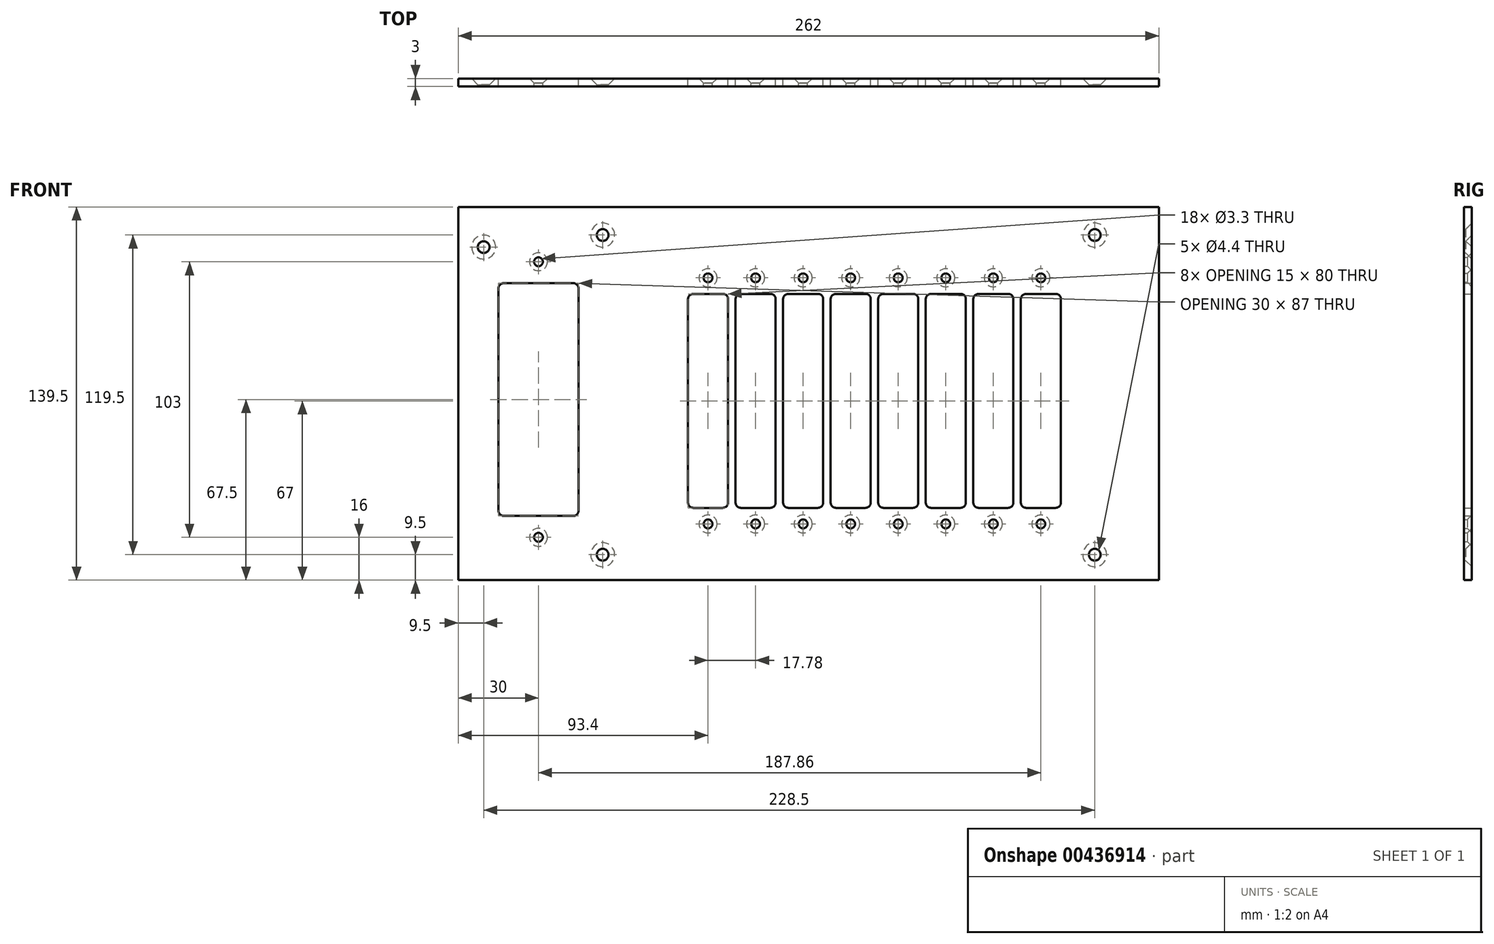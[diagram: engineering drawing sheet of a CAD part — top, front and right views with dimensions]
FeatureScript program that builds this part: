
annotation { "Feature Type Name" : "Feature", "Feature Type Description" : "" }
export const myFeature = defineFeature(function(context is Context, id is Id, definition is map)
    precondition{}
    {
        {
            var Q0;
            Q0=qCreatedBy(makeId("Front.planeOp"),FACE);
            var sketch = newSketch(context, id + "F0", { "sketchPlane" : qUnion([Q0])});
            skLineSegment(sketch, "E0.bottom", {"start": v(0, 0) * mm, "end": v(262, 0) * mm});
            skLineSegment(sketch, "E0.top", {"start": v(0, 139.5) * mm, "end": v(262, 139.5) * mm});
            skLineSegment(sketch, "E0.left", {"start": v(0, 0) * mm, "end": v(0, 139.5) * mm});
            skLineSegment(sketch, "E0.right", {"start": v(262, 0) * mm, "end": v(262, 139.5) * mm});
            skSolve(sketch);
        }
        {
            var Q0;
            Q0 = qSketchRegion(id + "F0", true);
            extrude(context, id + "F1", {"entities" : qUnion([Q0]), "depth" : 3 * mm});
        }
        {
            var Q0;
            Q0=makeQuery(id+"F1.opExtrude","CAP_FACE",FACE,{"disambiguationData":[OSD([sQuery(id+"F0.wireOp",EDGE,"E0.bottom"),sQuery(id+"F0.wireOp",EDGE,"E0.top"),sQuery(id+"F0.wireOp",EDGE,"E0.left"),sQuery(id+"F0.wireOp",EDGE,"E0.right"),sQuery(id+"F0.wireOp",EDGE,"e1765bbd-f1bd-4e84-b2cc-b87809b0bcc8.filletArc"),sQuery(id+"F0.wireOp",EDGE,"772ad9d4-1fb5-4f70-b089-cda75f8246e0.filletArc"),sQuery(id+"F0.wireOp",EDGE,"797730b0-c818-4667-b5a7-0f50415be0c5.filletArc"),sQuery(id+"F0.wireOp",EDGE,"a02b4f8d-2679-4b7b-95b5-bbf4c60ec907.filletArc")])],"isStart":true});
            var sketch = newSketch(context, id + "F2", { "sketchPlane" : qUnion([Q0])});
            skLineSegment(sketch, "E1.bottom", {"start": v(-43, 111) * mm, "end": v(-17, 111) * mm});
            skLineSegment(sketch, "E1.top", {"start": v(-43, 24) * mm, "end": v(-17, 24) * mm});
            skLineSegment(sketch, "E1.left", {"start": v(-45, 109) * mm, "end": v(-45, 26) * mm});
            skLineSegment(sketch, "E1.right", {"start": v(-15, 109) * mm, "end": v(-15, 26) * mm});
            skPoint(sketch, "E2.visualSharp", {"position": v(-45, 111) * mm});
            skArc(sketch, "E2.filletArc", {"start": v(-43, 111) * mm, "mid": v(-44.41, 110.41) * mm, "end": v(-45, 109) * mm});
            skPoint(sketch, "E3.visualSharp", {"position": v(-15, 111) * mm});
            skArc(sketch, "E3.filletArc", {"start": v(-15, 109) * mm, "mid": v(-15.59, 110.41) * mm, "end": v(-17, 111) * mm});
            skPoint(sketch, "E4.visualSharp", {"position": v(-15, 24) * mm});
            skArc(sketch, "E4.filletArc", {"start": v(-17, 24) * mm, "mid": v(-15.59, 24.59) * mm, "end": v(-15, 26) * mm});
            skPoint(sketch, "E5.visualSharp", {"position": v(-45, 24) * mm});
            skArc(sketch, "E5.filletArc", {"start": v(-45, 26) * mm, "mid": v(-44.41, 24.59) * mm, "end": v(-43, 24) * mm});
            skLineSegment(sketch, "E6", {"start": v(-30, 111) * mm, "end": v(-30, 24) * mm});
            skSolve(sketch);
        }
        {
            var Q0;
            Q0 = qSketchRegion(id + "F2", true);
            extrude(context, id + "F3", {"entities" : qUnion([Q0]), "operationType" : NewBodyOperationType.REMOVE, "endBound" : BoundingType.THROUGH_ALL, "oppositeDirection" : true, "depth" : 25 * mm});
        }
        {
            var Q0;
            Q0=makeQuery(id+"F1.opExtrude","CAP_FACE",FACE,{"disambiguationData":[OSD([sQuery(id+"F0.wireOp",EDGE,"E0.bottom"),sQuery(id+"F0.wireOp",EDGE,"E0.top"),sQuery(id+"F0.wireOp",EDGE,"E0.left"),sQuery(id+"F0.wireOp",EDGE,"E0.right"),sQuery(id+"F0.wireOp",EDGE,"e1765bbd-f1bd-4e84-b2cc-b87809b0bcc8.filletArc"),sQuery(id+"F0.wireOp",EDGE,"772ad9d4-1fb5-4f70-b089-cda75f8246e0.filletArc"),sQuery(id+"F0.wireOp",EDGE,"797730b0-c818-4667-b5a7-0f50415be0c5.filletArc"),sQuery(id+"F0.wireOp",EDGE,"a02b4f8d-2679-4b7b-95b5-bbf4c60ec907.filletArc")])],"isStart":true});
            var sketch = newSketch(context, id + "F4", { "sketchPlane" : qUnion([Q0])});
            skPoint(sketch, "E7", {"position": v(-30, 119) * mm});
            skPoint(sketch, "E7.positionSnap0", {"position": v(-30, 111) * mm});
            skPoint(sketch, "E8", {"position": v(-30, 16) * mm});
            skPoint(sketch, "E8.positionSnap0", {"position": v(-30, 24) * mm});
            skSolve(sketch);
        }
        {
            var Q0;
            Q0=sQuery(id+"F4.wireOp",VERTEX,"E7");
            var Q1;
            Q1=sQuery(id+"F4.wireOp",VERTEX,"E8");
            var Q2;
            Q2=makeQuery(id+"F1.opExtrude","SWEPT_BODY",BODY,{"disambiguationData":[OSD([sQuery(id+"F0.wireOp",EDGE,"E0.bottom"),sQuery(id+"F0.wireOp",EDGE,"E0.top"),sQuery(id+"F0.wireOp",EDGE,"E0.left"),sQuery(id+"F0.wireOp",EDGE,"E0.right"),sQuery(id+"F0.wireOp",EDGE,"e1765bbd-f1bd-4e84-b2cc-b87809b0bcc8.filletArc"),sQuery(id+"F0.wireOp",EDGE,"772ad9d4-1fb5-4f70-b089-cda75f8246e0.filletArc"),sQuery(id+"F0.wireOp",EDGE,"797730b0-c818-4667-b5a7-0f50415be0c5.filletArc"),sQuery(id+"F0.wireOp",EDGE,"a02b4f8d-2679-4b7b-95b5-bbf4c60ec907.filletArc")])]});
            hole(context, id + "F5", {"style" : HoleStyle.C_SINK, "endStyle" : HoleEndStyle.THROUGH, "standardTappedOrClearance" : lookupTablePath({ "standard" : "ISO", "fit" : "Normal", "size" : "M3", "type" : "Clearance" }), "standardBlindInLast" : lookupTablePath({ "fit" : "Standard", "standard" : "ISO", "size" : "M3", "type" : "Clearance" }), "holeDiameter" : 3.3 * mm, "cSinkDiameter" : 6.72 * mm, "cSinkAngle" : 90 * degree, "isTappedThrough" : true, "tappedDepth" : 12 * mm, "tapClearance" : 3, "locations" : qUnion([Q0, Q1]), "scope" : qUnion([Q2])});
        }
        {
            var Q0;
            Q0=makeQuery(id+"F1.opExtrude","CAP_FACE",FACE,{"disambiguationData":[OSD([sQuery(id+"F0.wireOp",EDGE,"E0.bottom"),sQuery(id+"F0.wireOp",EDGE,"E0.top"),sQuery(id+"F0.wireOp",EDGE,"E0.left"),sQuery(id+"F0.wireOp",EDGE,"E0.right"),sQuery(id+"F0.wireOp",EDGE,"e1765bbd-f1bd-4e84-b2cc-b87809b0bcc8.filletArc"),sQuery(id+"F0.wireOp",EDGE,"772ad9d4-1fb5-4f70-b089-cda75f8246e0.filletArc"),sQuery(id+"F0.wireOp",EDGE,"797730b0-c818-4667-b5a7-0f50415be0c5.filletArc"),sQuery(id+"F0.wireOp",EDGE,"a02b4f8d-2679-4b7b-95b5-bbf4c60ec907.filletArc")])],"isStart":true});
            var sketch = newSketch(context, id + "F6", { "sketchPlane" : qUnion([Q0])});
            skLineSegment(sketch, "E9.bottom", {"start": v(-87.9, 27) * mm, "end": v(-98.9, 27) * mm});
            skLineSegment(sketch, "E9.top", {"start": v(-87.9, 107) * mm, "end": v(-98.9, 107) * mm});
            skLineSegment(sketch, "E9.left", {"start": v(-85.9, 29) * mm, "end": v(-85.9, 105) * mm});
            skLineSegment(sketch, "E9.right", {"start": v(-100.9, 29) * mm, "end": v(-100.9, 105) * mm});
            skPoint(sketch, "E10.visualSharp", {"position": v(-100.9, 107) * mm});
            skArc(sketch, "E10.filletArc", {"start": v(-98.9, 107) * mm, "mid": v(-100.31, 106.41) * mm, "end": v(-100.9, 105) * mm});
            skPoint(sketch, "E11.visualSharp", {"position": v(-85.9, 107) * mm});
            skArc(sketch, "E11.filletArc", {"start": v(-85.9, 105) * mm, "mid": v(-86.49, 106.41) * mm, "end": v(-87.9, 107) * mm});
            skPoint(sketch, "E12.visualSharp", {"position": v(-85.9, 27) * mm});
            skArc(sketch, "E12.filletArc", {"start": v(-87.9, 27) * mm, "mid": v(-86.49, 27.59) * mm, "end": v(-85.9, 29) * mm});
            skPoint(sketch, "E13.visualSharp", {"position": v(-100.9, 27) * mm});
            skArc(sketch, "E13.filletArc", {"start": v(-100.9, 29) * mm, "mid": v(-100.31, 27.59) * mm, "end": v(-98.9, 27) * mm});
            skLineSegment(sketch, "E14.1.0.0", {"start": v(-105.68, 107) * mm, "end": v(-116.68, 107) * mm});
            skLineSegment(sketch, "E14.1.0.1", {"start": v(-105.68, 27) * mm, "end": v(-116.68, 27) * mm});
            skPoint(sketch, "E14.1.0.2", {"position": v(-118.68, 107) * mm});
            skPoint(sketch, "E14.1.0.3", {"position": v(-103.68, 107) * mm});
            skPoint(sketch, "E14.1.0.4", {"position": v(-103.68, 27) * mm});
            skPoint(sketch, "E14.1.0.5", {"position": v(-118.68, 27) * mm});
            skLineSegment(sketch, "E14.1.0.6", {"start": v(-103.68, 29) * mm, "end": v(-103.68, 105) * mm});
            skLineSegment(sketch, "E14.1.0.7", {"start": v(-118.68, 29) * mm, "end": v(-118.68, 105) * mm});
            skArc(sketch, "E14.1.0.8", {"start": v(-116.68, 107) * mm, "mid": v(-118.1, 106.41) * mm, "end": v(-118.68, 105) * mm});
            skArc(sketch, "E14.1.0.9", {"start": v(-103.68, 105) * mm, "mid": v(-104.27, 106.41) * mm, "end": v(-105.68, 107) * mm});
            skArc(sketch, "E14.1.0.10", {"start": v(-105.68, 27) * mm, "mid": v(-104.27, 27.59) * mm, "end": v(-103.68, 29) * mm});
            skArc(sketch, "E14.1.0.11", {"start": v(-118.68, 29) * mm, "mid": v(-118.1, 27.59) * mm, "end": v(-116.68, 27) * mm});
            skLineSegment(sketch, "E14.2.0.0", {"start": v(-123.46, 107) * mm, "end": v(-134.46, 107) * mm});
            skLineSegment(sketch, "E14.2.0.1", {"start": v(-123.46, 27) * mm, "end": v(-134.46, 27) * mm});
            skPoint(sketch, "E14.2.0.2", {"position": v(-136.46, 107) * mm});
            skPoint(sketch, "E14.2.0.3", {"position": v(-121.46, 107) * mm});
            skPoint(sketch, "E14.2.0.4", {"position": v(-121.46, 27) * mm});
            skPoint(sketch, "E14.2.0.5", {"position": v(-136.46, 27) * mm});
            skLineSegment(sketch, "E14.2.0.6", {"start": v(-121.46, 29) * mm, "end": v(-121.46, 105) * mm});
            skLineSegment(sketch, "E14.2.0.7", {"start": v(-136.46, 29) * mm, "end": v(-136.46, 105) * mm});
            skArc(sketch, "E14.2.0.8", {"start": v(-134.46, 107) * mm, "mid": v(-135.87, 106.41) * mm, "end": v(-136.46, 105) * mm});
            skArc(sketch, "E14.2.0.9", {"start": v(-121.46, 105) * mm, "mid": v(-122.05, 106.41) * mm, "end": v(-123.46, 107) * mm});
            skArc(sketch, "E14.2.0.10", {"start": v(-123.46, 27) * mm, "mid": v(-122.05, 27.59) * mm, "end": v(-121.46, 29) * mm});
            skArc(sketch, "E14.2.0.11", {"start": v(-136.46, 29) * mm, "mid": v(-135.87, 27.59) * mm, "end": v(-134.46, 27) * mm});
            skLineSegment(sketch, "E14.3.0.0", {"start": v(-141.24, 107) * mm, "end": v(-152.24, 107) * mm});
            skLineSegment(sketch, "E14.3.0.1", {"start": v(-141.24, 27) * mm, "end": v(-152.24, 27) * mm});
            skPoint(sketch, "E14.3.0.2", {"position": v(-154.24, 107) * mm});
            skPoint(sketch, "E14.3.0.3", {"position": v(-139.24, 107) * mm});
            skPoint(sketch, "E14.3.0.4", {"position": v(-139.24, 27) * mm});
            skPoint(sketch, "E14.3.0.5", {"position": v(-154.24, 27) * mm});
            skLineSegment(sketch, "E14.3.0.6", {"start": v(-139.24, 29) * mm, "end": v(-139.24, 105) * mm});
            skLineSegment(sketch, "E14.3.0.7", {"start": v(-154.24, 29) * mm, "end": v(-154.24, 105) * mm});
            skArc(sketch, "E14.3.0.8", {"start": v(-152.24, 107) * mm, "mid": v(-153.65, 106.41) * mm, "end": v(-154.24, 105) * mm});
            skArc(sketch, "E14.3.0.9", {"start": v(-139.24, 105) * mm, "mid": v(-139.83, 106.41) * mm, "end": v(-141.24, 107) * mm});
            skArc(sketch, "E14.3.0.10", {"start": v(-141.24, 27) * mm, "mid": v(-139.83, 27.59) * mm, "end": v(-139.24, 29) * mm});
            skArc(sketch, "E14.3.0.11", {"start": v(-154.24, 29) * mm, "mid": v(-153.65, 27.59) * mm, "end": v(-152.24, 27) * mm});
            skLineSegment(sketch, "E14.4.0.0", {"start": v(-159.02, 107) * mm, "end": v(-170.02, 107) * mm});
            skLineSegment(sketch, "E14.4.0.1", {"start": v(-159.02, 27) * mm, "end": v(-170.02, 27) * mm});
            skPoint(sketch, "E14.4.0.2", {"position": v(-172.02, 107) * mm});
            skPoint(sketch, "E14.4.0.3", {"position": v(-157.02, 107) * mm});
            skPoint(sketch, "E14.4.0.4", {"position": v(-157.02, 27) * mm});
            skPoint(sketch, "E14.4.0.5", {"position": v(-172.02, 27) * mm});
            skLineSegment(sketch, "E14.4.0.6", {"start": v(-157.02, 29) * mm, "end": v(-157.02, 105) * mm});
            skLineSegment(sketch, "E14.4.0.7", {"start": v(-172.02, 29) * mm, "end": v(-172.02, 105) * mm});
            skArc(sketch, "E14.4.0.8", {"start": v(-170.02, 107) * mm, "mid": v(-171.43, 106.41) * mm, "end": v(-172.02, 105) * mm});
            skArc(sketch, "E14.4.0.9", {"start": v(-157.02, 105) * mm, "mid": v(-157.6, 106.41) * mm, "end": v(-159.02, 107) * mm});
            skArc(sketch, "E14.4.0.10", {"start": v(-159.02, 27) * mm, "mid": v(-157.6, 27.59) * mm, "end": v(-157.02, 29) * mm});
            skArc(sketch, "E14.4.0.11", {"start": v(-172.02, 29) * mm, "mid": v(-171.43, 27.59) * mm, "end": v(-170.02, 27) * mm});
            skLineSegment(sketch, "E14.5.0.0", {"start": v(-176.8, 107) * mm, "end": v(-187.8, 107) * mm});
            skLineSegment(sketch, "E14.5.0.1", {"start": v(-176.8, 27) * mm, "end": v(-187.8, 27) * mm});
            skPoint(sketch, "E14.5.0.2", {"position": v(-189.8, 107) * mm});
            skPoint(sketch, "E14.5.0.3", {"position": v(-174.8, 107) * mm});
            skPoint(sketch, "E14.5.0.4", {"position": v(-174.8, 27) * mm});
            skPoint(sketch, "E14.5.0.5", {"position": v(-189.8, 27) * mm});
            skLineSegment(sketch, "E14.5.0.6", {"start": v(-174.8, 29) * mm, "end": v(-174.8, 105) * mm});
            skLineSegment(sketch, "E14.5.0.7", {"start": v(-189.8, 29) * mm, "end": v(-189.8, 105) * mm});
            skArc(sketch, "E14.5.0.8", {"start": v(-187.8, 107) * mm, "mid": v(-189.21, 106.41) * mm, "end": v(-189.8, 105) * mm});
            skArc(sketch, "E14.5.0.9", {"start": v(-174.8, 105) * mm, "mid": v(-175.39, 106.41) * mm, "end": v(-176.8, 107) * mm});
            skArc(sketch, "E14.5.0.10", {"start": v(-176.8, 27) * mm, "mid": v(-175.39, 27.59) * mm, "end": v(-174.8, 29) * mm});
            skArc(sketch, "E14.5.0.11", {"start": v(-189.8, 29) * mm, "mid": v(-189.21, 27.59) * mm, "end": v(-187.8, 27) * mm});
            skLineSegment(sketch, "E14.direction1", {"start": v(-100.9, 27) * mm, "end": v(-118.68, 27) * mm, "construction": true});
            skPoint(sketch, "E15", {"position": v(-93.4, 113) * mm});
            skPoint(sketch, "E15.positionSnap0", {"position": v(-93.4, 107) * mm});
            skPoint(sketch, "E16", {"position": v(-93.4, 21) * mm});
            skPoint(sketch, "E16.positionSnap0", {"position": v(-93.4, 27) * mm});
            skLineSegment(sketch, "E17.0.6.0", {"start": v(-194.58, 107) * mm, "end": v(-205.58, 107) * mm});
            skLineSegment(sketch, "E17.3.6.0", {"start": v(-194.58, 27) * mm, "end": v(-205.58, 27) * mm});
            skPoint(sketch, "E17.6.6.0", {"position": v(-207.58, 107) * mm});
            skPoint(sketch, "E17.7.6.0", {"position": v(-192.58, 107) * mm});
            skPoint(sketch, "E17.8.6.0", {"position": v(-192.58, 27) * mm});
            skPoint(sketch, "E17.9.6.0", {"position": v(-207.58, 27) * mm});
            skLineSegment(sketch, "E17.10.6.0", {"start": v(-192.58, 29) * mm, "end": v(-192.58, 105) * mm});
            skLineSegment(sketch, "E17.13.6.0", {"start": v(-207.58, 29) * mm, "end": v(-207.58, 105) * mm});
            skArc(sketch, "E17.16.6.0", {"start": v(-205.58, 107) * mm, "mid": v(-207, 106.41) * mm, "end": v(-207.58, 105) * mm});
            skArc(sketch, "E17.20.6.0", {"start": v(-192.58, 105) * mm, "mid": v(-193.17, 106.41) * mm, "end": v(-194.58, 107) * mm});
            skArc(sketch, "E17.24.6.0", {"start": v(-194.58, 27) * mm, "mid": v(-193.17, 27.59) * mm, "end": v(-192.58, 29) * mm});
            skArc(sketch, "E17.28.6.0", {"start": v(-207.58, 29) * mm, "mid": v(-207, 27.59) * mm, "end": v(-205.58, 27) * mm});
            skLineSegment(sketch, "E17.0.7.0", {"start": v(-212.36, 107) * mm, "end": v(-223.36, 107) * mm});
            skLineSegment(sketch, "E17.3.7.0", {"start": v(-212.36, 27) * mm, "end": v(-223.36, 27) * mm});
            skPoint(sketch, "E17.6.7.0", {"position": v(-225.36, 107) * mm});
            skPoint(sketch, "E17.7.7.0", {"position": v(-210.36, 107) * mm});
            skPoint(sketch, "E17.8.7.0", {"position": v(-210.36, 27) * mm});
            skPoint(sketch, "E17.9.7.0", {"position": v(-225.36, 27) * mm});
            skLineSegment(sketch, "E17.10.7.0", {"start": v(-210.36, 29) * mm, "end": v(-210.36, 105) * mm});
            skLineSegment(sketch, "E17.13.7.0", {"start": v(-225.36, 29) * mm, "end": v(-225.36, 105) * mm});
            skArc(sketch, "E17.16.7.0", {"start": v(-223.36, 107) * mm, "mid": v(-224.77, 106.41) * mm, "end": v(-225.36, 105) * mm});
            skArc(sketch, "E17.20.7.0", {"start": v(-210.36, 105) * mm, "mid": v(-210.95, 106.41) * mm, "end": v(-212.36, 107) * mm});
            skArc(sketch, "E17.24.7.0", {"start": v(-212.36, 27) * mm, "mid": v(-210.95, 27.59) * mm, "end": v(-210.36, 29) * mm});
            skArc(sketch, "E17.28.7.0", {"start": v(-225.36, 29) * mm, "mid": v(-224.77, 27.59) * mm, "end": v(-223.36, 27) * mm});
            skPoint(sketch, "E18.1.0.0", {"position": v(-111.18, 113) * mm});
            skPoint(sketch, "E18.1.0.1", {"position": v(-111.18, 21) * mm});
            skPoint(sketch, "E18.2.0.0", {"position": v(-128.96, 113) * mm});
            skPoint(sketch, "E18.2.0.1", {"position": v(-128.96, 21) * mm});
            skPoint(sketch, "E18.3.0.0", {"position": v(-146.74, 113) * mm});
            skPoint(sketch, "E18.3.0.1", {"position": v(-146.74, 21) * mm});
            skPoint(sketch, "E18.4.0.0", {"position": v(-164.52, 113) * mm});
            skPoint(sketch, "E18.4.0.1", {"position": v(-164.52, 21) * mm});
            skPoint(sketch, "E18.5.0.0", {"position": v(-182.3, 113) * mm});
            skPoint(sketch, "E18.5.0.1", {"position": v(-182.3, 21) * mm});
            skPoint(sketch, "E18.6.0.0", {"position": v(-200.08, 113) * mm});
            skPoint(sketch, "E18.6.0.1", {"position": v(-200.08, 21) * mm});
            skPoint(sketch, "E18.7.0.0", {"position": v(-217.86, 113) * mm});
            skPoint(sketch, "E18.7.0.1", {"position": v(-217.86, 21) * mm});
            skLineSegment(sketch, "E18.direction1", {"start": v(-93.4, 113) * mm, "end": v(-111.18, 113) * mm, "construction": true});
            skSolve(sketch);
        }
        {
            var Q0;
            Q0=sQuery(id+"F6.wireOp",VERTEX,"E18.7.0.0");
            var Q1;
            Q1=sQuery(id+"F6.wireOp",VERTEX,"E18.6.0.0");
            var Q2;
            Q2=sQuery(id+"F6.wireOp",VERTEX,"E18.5.0.0");
            var Q3;
            Q3=sQuery(id+"F6.wireOp",VERTEX,"E18.4.0.0");
            var Q4;
            Q4=sQuery(id+"F6.wireOp",VERTEX,"E18.3.0.0");
            var Q5;
            Q5=sQuery(id+"F6.wireOp",VERTEX,"E18.2.0.0");
            var Q6;
            Q6=sQuery(id+"F6.wireOp",VERTEX,"E18.1.0.0");
            var Q7;
            Q7=sQuery(id+"F6.wireOp",VERTEX,"E15");
            var Q8;
            Q8=sQuery(id+"F6.wireOp",VERTEX,"E16");
            var Q9;
            Q9=sQuery(id+"F6.wireOp",VERTEX,"E18.1.0.1");
            var Q10;
            Q10=sQuery(id+"F6.wireOp",VERTEX,"E18.3.0.1");
            var Q11;
            Q11=sQuery(id+"F6.wireOp",VERTEX,"E18.4.0.1");
            var Q12;
            Q12=sQuery(id+"F6.wireOp",VERTEX,"E18.2.0.1");
            var Q13;
            Q13=sQuery(id+"F6.wireOp",VERTEX,"E18.5.0.1");
            var Q14;
            Q14=sQuery(id+"F6.wireOp",VERTEX,"E18.7.0.1");
            var Q15;
            Q15=sQuery(id+"F6.wireOp",VERTEX,"E18.6.0.1");
            var Q16;
            Q16=makeQuery(id+"F1.opExtrude","SWEPT_BODY",BODY,{"disambiguationData":[OSD([sQuery(id+"F0.wireOp",EDGE,"E0.bottom"),sQuery(id+"F0.wireOp",EDGE,"E0.top"),sQuery(id+"F0.wireOp",EDGE,"E0.left"),sQuery(id+"F0.wireOp",EDGE,"E0.right")])]});
            hole(context, id + "F7", {"style" : HoleStyle.C_SINK, "endStyle" : HoleEndStyle.THROUGH, "standardTappedOrClearance" : lookupTablePath({ "standard" : "ISO", "fit" : "Normal", "size" : "M3", "type" : "Clearance" }), "standardBlindInLast" : lookupTablePath({ "fit" : "Standard", "standard" : "ISO", "size" : "M3", "type" : "Clearance" }), "holeDiameter" : 3.3 * mm, "cSinkDiameter" : 6.72 * mm, "cSinkAngle" : 90 * degree, "isTappedThrough" : true, "tappedDepth" : 12 * mm, "tapClearance" : 3, "locations" : qUnion([Q0, Q1, Q2, Q3, Q4, Q5, Q6, Q7, Q8, Q9, Q10, Q11, Q12, Q13, Q14, Q15]), "scope" : qUnion([Q16])});
        }
        {
            var Q0;
            Q0 = qSketchRegion(id + "F6", true);
            extrude(context, id + "F8", {"entities" : qUnion([Q0]), "operationType" : NewBodyOperationType.REMOVE, "endBound" : BoundingType.THROUGH_ALL, "oppositeDirection" : true, "depth" : 25 * mm});
        }
        {
            var Q0;
            Q0=makeQuery(id+"F1.opExtrude","CAP_FACE",FACE,{"disambiguationData":[OSD([sQuery(id+"F0.wireOp",EDGE,"E0.bottom"),sQuery(id+"F0.wireOp",EDGE,"E0.top"),sQuery(id+"F0.wireOp",EDGE,"E0.left"),sQuery(id+"F0.wireOp",EDGE,"E0.right"),sQuery(id+"F0.wireOp",EDGE,"e1765bbd-f1bd-4e84-b2cc-b87809b0bcc8.filletArc"),sQuery(id+"F0.wireOp",EDGE,"772ad9d4-1fb5-4f70-b089-cda75f8246e0.filletArc"),sQuery(id+"F0.wireOp",EDGE,"797730b0-c818-4667-b5a7-0f50415be0c5.filletArc"),sQuery(id+"F0.wireOp",EDGE,"a02b4f8d-2679-4b7b-95b5-bbf4c60ec907.filletArc")])],"isStart":true});
            var sketch = newSketch(context, id + "F9", { "sketchPlane" : qUnion([Q0])});
            skPoint(sketch, "E19", {"position": v(-9.5, 124.5) * mm});
            skPoint(sketch, "E20", {"position": v(-238, 129) * mm});
            skPoint(sketch, "E21", {"position": v(-54, 129) * mm});
            skPoint(sketch, "E22", {"position": v(-238, 9.5) * mm});
            skPoint(sketch, "E23", {"position": v(-54, 9.5) * mm});
            skSolve(sketch);
        }
        {
            var Q0;
            Q0=sQuery(id+"F9.wireOp",VERTEX,"E19");
            var Q1;
            Q1=sQuery(id+"F9.wireOp",VERTEX,"E20");
            var Q2;
            Q2=sQuery(id+"F9.wireOp",VERTEX,"E21");
            var Q3;
            Q3=sQuery(id+"F9.wireOp",VERTEX,"E22");
            var Q4;
            Q4=sQuery(id+"F9.wireOp",VERTEX,"E23");
            var Q5;
            Q5=makeQuery(id+"F1.opExtrude","SWEPT_BODY",BODY,{"disambiguationData":[OSD([sQuery(id+"F0.wireOp",EDGE,"E0.bottom"),sQuery(id+"F0.wireOp",EDGE,"E0.top"),sQuery(id+"F0.wireOp",EDGE,"E0.left"),sQuery(id+"F0.wireOp",EDGE,"E0.right"),sQuery(id+"F0.wireOp",EDGE,"e1765bbd-f1bd-4e84-b2cc-b87809b0bcc8.filletArc"),sQuery(id+"F0.wireOp",EDGE,"772ad9d4-1fb5-4f70-b089-cda75f8246e0.filletArc"),sQuery(id+"F0.wireOp",EDGE,"797730b0-c818-4667-b5a7-0f50415be0c5.filletArc"),sQuery(id+"F0.wireOp",EDGE,"a02b4f8d-2679-4b7b-95b5-bbf4c60ec907.filletArc")])]});
            hole(context, id + "F10", {"style" : HoleStyle.C_SINK, "endStyle" : HoleEndStyle.THROUGH, "standardTappedOrClearance" : lookupTablePath({ "standard" : "ISO", "fit" : "Normal", "size" : "M4", "type" : "Clearance" }), "standardBlindInLast" : lookupTablePath({ "fit" : "Standard", "standard" : "ISO", "size" : "M4", "type" : "Clearance" }), "holeDiameter" : 4.4 * mm, "cSinkDiameter" : 8.96 * mm, "cSinkAngle" : 90 * degree, "isTappedThrough" : true, "tappedDepth" : 12 * mm, "tapClearance" : 3, "locations" : qUnion([Q0, Q1, Q2, Q3, Q4]), "scope" : qUnion([Q5])});
        }
    });
